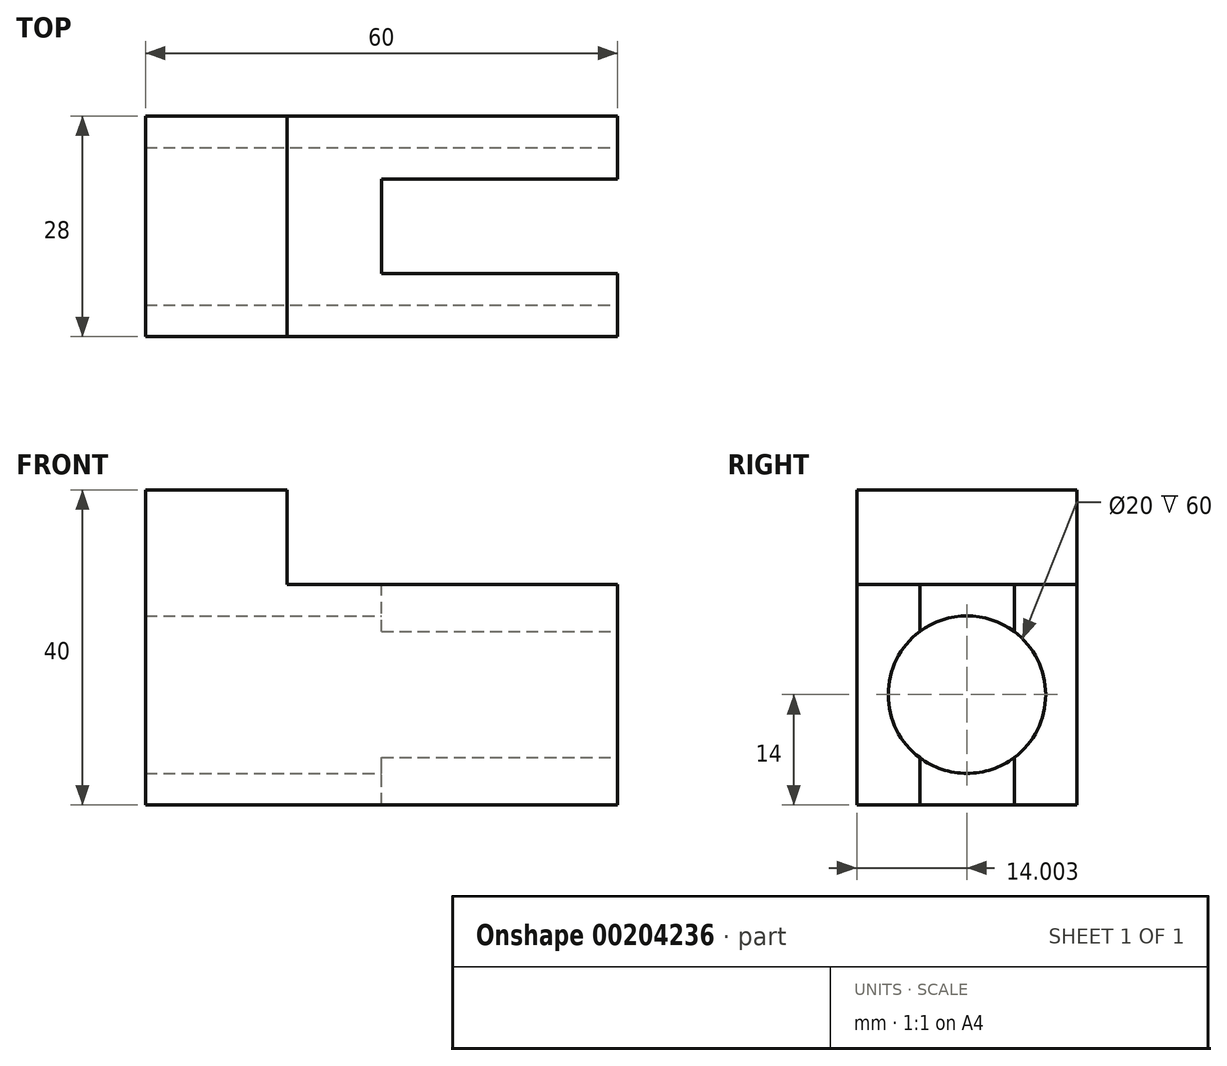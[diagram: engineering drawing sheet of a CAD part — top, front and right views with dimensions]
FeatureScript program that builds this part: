
annotation { "Feature Type Name" : "Feature", "Feature Type Description" : "" }
export const myFeature = defineFeature(function(context is Context, id is Id, definition is map)
    precondition{}
    {
        {
            var Q0;
            Q0=qCreatedBy(makeId("Top.planeOp"),FACE);
            var sketch = newSketch(context, id + "F0", { "sketchPlane" : qUnion([Q0])});
            skLineSegment(sketch, "E0", {"start": v(-58.56, -39.9) * mm, "end": v(1.44, -39.9) * mm});
            skLineSegment(sketch, "E1", {"start": v(1.44, -39.9) * mm, "end": v(1.44, -11.9) * mm});
            skLineSegment(sketch, "E2", {"start": v(1.44, -11.9) * mm, "end": v(-58.56, -11.9) * mm});
            skLineSegment(sketch, "E3", {"start": v(-58.56, -11.9) * mm, "end": v(-58.56, -39.9) * mm});
            skSolve(sketch);
        }
        {
            var Q0;
            Q0 = qSketchRegion(id + "F0", true);
            extrude(context, id + "F1", {"entities" : qUnion([Q0]), "depth" : 40 * mm});
        }
        {
            var Q0;
            Q0=makeQuery(id+"F1.opExtrude","CAP_FACE",FACE,{"disambiguationData":[OSD([sQuery(id+"F0.wireOp",EDGE,"E0"),sQuery(id+"F0.wireOp",EDGE,"E1"),sQuery(id+"F0.wireOp",EDGE,"E2"),sQuery(id+"F0.wireOp",EDGE,"E3")])],"isStart":false});
            var sketch = newSketch(context, id + "F2", { "sketchPlane" : qUnion([Q0])});
            skLineSegment(sketch, "E4", {"start": v(1.44, -39.9) * mm, "end": v(1.44, -11.9) * mm});
            skLineSegment(sketch, "E5", {"start": v(1.44, -11.9) * mm, "end": v(-40.56, -11.9) * mm});
            skLineSegment(sketch, "E6", {"start": v(-40.56, -11.9) * mm, "end": v(-40.56, -39.9) * mm});
            skLineSegment(sketch, "E7", {"start": v(-40.56, -39.9) * mm, "end": v(1.44, -39.9) * mm});
            skSolve(sketch);
        }
        {
            var Q0;
            Q0=makeQuery(id+"F2.imprint","IMPRINT",FACE,{"disambiguationData":[TD([[makeQuery(id+"F2.imprint","IMPRINT",EDGE,{"derivedFrom":sQuery(id+"F2.wireOp",EDGE,"E4")}),1.0]])]});
            extrude(context, id + "F3", {"entities" : qUnion([Q0]), "operationType" : NewBodyOperationType.REMOVE, "oppositeDirection" : true, "depth" : 12 * mm});
        }
        {
            var Q0;
            Q0=makeQuery(id+"F1.opExtrude","SWEPT_FACE",FACE,{"disambiguationData":[OSD([sQuery(id+"F0.wireOp",EDGE,"E1")])]});
            var sketch = newSketch(context, id + "F4", { "sketchPlane" : qUnion([Q0])});
            skPoint(sketch, "E8.endSnap0", {"position": v(-25.9, 28) * mm});
            skCircle(sketch, "E9", {"center": v(-25.9, 14) * mm, "radius": 10 * mm});
            skSolve(sketch);
        }
        {
            var Q0;
            Q0=makeQuery(id+"F4.imprint","IMPRINT",FACE,{"disambiguationData":[TD([[makeQuery(id+"F4.imprint","IMPRINT",EDGE,{"derivedFrom":sQuery(id+"F4.wireOp",EDGE,"E9")}),1.0]])]});
            extrude(context, id + "F5", {"entities" : qUnion([Q0]), "operationType" : NewBodyOperationType.REMOVE, "oppositeDirection" : true, "depth" : 60 * mm});
        }
        {
            var Q0;
            Q0=makeQuery(id+"F1.opExtrude","SWEPT_FACE",FACE,{"disambiguationData":[OSD([sQuery(id+"F0.wireOp",EDGE,"E1")])]});
            var sketch = newSketch(context, id + "F6", { "sketchPlane" : qUnion([Q0])});
            skLineSegment(sketch, "E10", {"start": v(-31.9, 0) * mm, "end": v(-19.9, 0) * mm});
            skLineSegment(sketch, "E11", {"start": v(-19.9, 0) * mm, "end": v(-19.9, 28) * mm});
            skLineSegment(sketch, "E12", {"start": v(-19.9, 28) * mm, "end": v(-31.9, 28) * mm});
            skLineSegment(sketch, "E13", {"start": v(-31.9, 28) * mm, "end": v(-31.9, 0) * mm});
            skSolve(sketch);
        }
        {
            var Q0;
            {var subQ0=sQuery(id+"F6.wireOp",EDGE,"E10");Q0=makeQuery(id+"F6.imprint","IMPRINT",FACE,{"disambiguationData":[TD([[makeQuery(id+"F6.imprint","IMPRINT",EDGE,{"derivedFrom":subQ0}),1.0]])]});}
            var Q1;
            {var subQ0=sQuery(id+"F6.wireOp",EDGE,"E12");Q1=makeQuery(id+"F6.imprint","IMPRINT",FACE,{"disambiguationData":[TD([[makeQuery(id+"F6.imprint","IMPRINT",EDGE,{"derivedFrom":subQ0}),-1.0]])]});}
            extrude(context, id + "F7", {"entities" : qUnion([Q0, Q1]), "operationType" : NewBodyOperationType.REMOVE, "oppositeDirection" : true, "depth" : 30 * mm});
        }
    });
